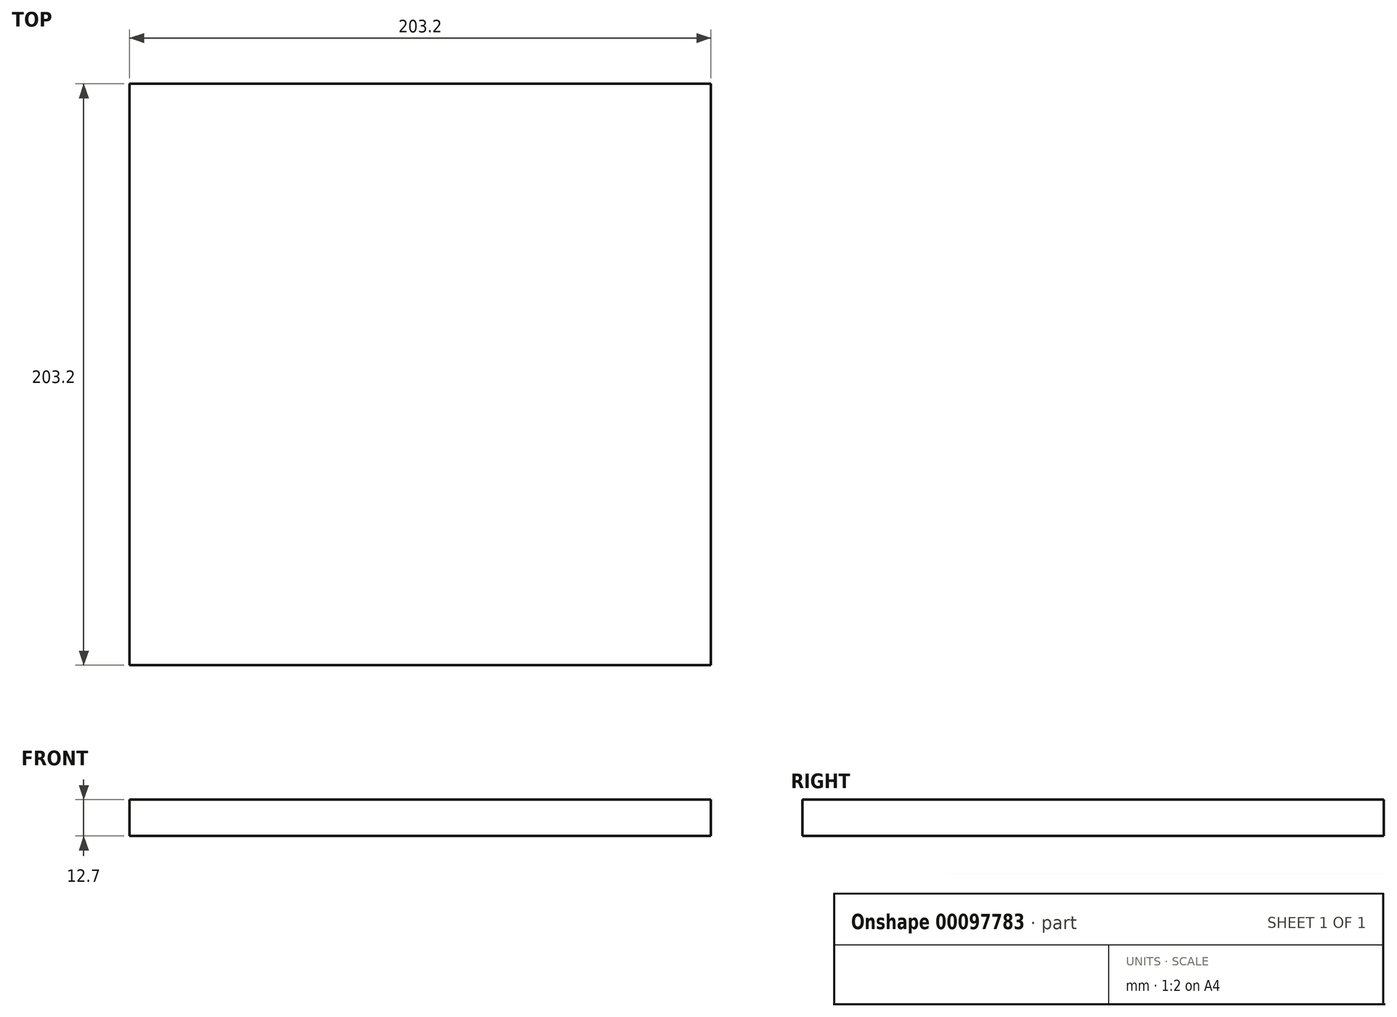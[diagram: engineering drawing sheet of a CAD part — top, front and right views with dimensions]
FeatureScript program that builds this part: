
annotation { "Feature Type Name" : "Feature", "Feature Type Description" : "" }
export const myFeature = defineFeature(function(context is Context, id is Id, definition is map)
    precondition{}
    {
        {
            var Q0;
            Q0=qCreatedBy(makeId("Top.planeOp"),FACE);
            var sketch = newSketch(context, id + "F0", { "sketchPlane" : qUnion([Q0])});
            skLineSegment(sketch, "E0.bottom", {"start": v(-101.6, 101.6) * mm, "end": v(101.6, 101.6) * mm});
            skLineSegment(sketch, "E0.top", {"start": v(-101.6, -101.6) * mm, "end": v(101.6, -101.6) * mm});
            skLineSegment(sketch, "E0.left", {"start": v(-101.6, 101.6) * mm, "end": v(-101.6, -101.6) * mm});
            skLineSegment(sketch, "E0.right", {"start": v(101.6, 101.6) * mm, "end": v(101.6, -101.6) * mm});
            skPoint(sketch, "E0.middle", {"position": v(0, 0) * mm});
            skSolve(sketch);
        }
        {
            var Q0;
            Q0=makeQuery(id+"F0.imprint","IMPRINT",FACE,{"disambiguationData":[TD([[makeQuery(id+"F0.imprint","IMPRINT",EDGE,{"derivedFrom":sQuery(id+"F0.wireOp",EDGE,"E0.bottom")}),-1.0]])]});
            extrude(context, id + "F1", {"entities" : qUnion([Q0]), "depth" : 12.7 * mm});
        }
    });
